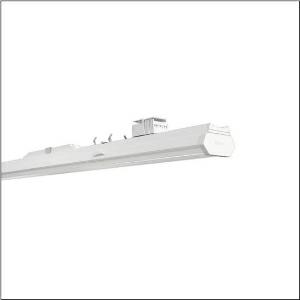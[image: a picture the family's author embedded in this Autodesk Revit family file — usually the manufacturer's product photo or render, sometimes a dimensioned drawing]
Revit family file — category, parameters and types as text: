
# Revit family: licross_r__11_protected_mo_51tp12dn495g3c_6ec9
name_source: partatom
category: Lighting Fixtures
units: mm (PartAtom-declared; Revit-internal decimal feet)

## family parameters
Cut with Voids When Loaded = No
Host = Face
Light Source = No
Part Type = Normal
Room Calculation Point = No
Round Connector Dimension = Use Diameter
Shared = No

## types (1)
- --- (1 x LED, 980 lm, 6.8 W, 4000K)
    Apparent Load = 7 VA
    CIE Flux Codes = 73 92 98 99 100
    Color Rendering = 80
    Color Temperature = 4000K
    Default Elevation = 1800 mm
    Description = Licross® 11 Protected MO, luminaire insert, of sheet steel, galvanised, coil coated, white, length: 1.500mm, width: 90mm, height: 101mm, LED rated luminous flux: 9.980lm, light colour: 840, control gear: DALI 2 (for two DALI lines), with plug, 6-pole, with phase selection, for trunking rail, 14-core, mains connection: 220..240V, AC, 50/60Hz, rated input power: 61W, for trunking rail, 14-core, internal wiring halogen-free, for emergency light function, converter,control gear: single battery element, battery: LiFePO4, 9Ah, primary light control with lens, of plastic, primary optical cover: cover, of PMMA, light emission: direct distribution, primary light characteristic: symmetric, protection rating (complete): IP64, insulation class (complete): insulation class I (protective earthing), certification: CE, UKCA, protection symbol: D if used in an environment with conductive dust loads with corresponding accessories, impact resistance: IK06, permissible ambient temperature for indoor applications: +5..+35°C, standard: EN 60598-2-22, LABS conformity tested according to VDMA 24364:2018-05, reducing of maximum allowable ambient temperature of 5°C with ceiling mounting, corresponds to IFS (International Featured Standards) requirements for safety and quality in the food industry, packaging unit: 1 piece
    Height = 92 mm
    Lamp = 1 x LED
    Lamp Light Flux = 980 lm
    Lamp Power = 6.8 W
    Lamp count = 1
    Length = 1500 mm
    Luminous efficacy = 144 lm/W
    Manufacturer = Siteco
    ModVariant = No
    Model = 51TP12DN495G3C
    Mounting Place = Ceiling
    Mounting Type = Pendant
    Number of Poles = 1
    OnlyDefault = Yes
    Power Factor = 1
    Product Name = Licross® 11 Protected MO
    Product group = luminaire insert | ceiling pendant
    ProductGroupID = 902
    Protection Class = Protection class I
    Protection Degree = IP 64
    RLX_Detail_Level = 1
    RLX_Emergency_Light_Flux = 0 lm
    RLX_Emergency_Type = 0
    RLX_Emergency_Type_DB = No
    RlxData = <blob elided: 24809 chars, md5=9ab4ca81>
    Socket = socket
    Standby Power = 0 W
    System Light Flux = 980 lm
    System Power = 7 W
    Type Comments = : emergency light operation: 3 h
    Type Image = l_1256148.jpg
    URL = http://relux.com
    VarID = @adj_112189
    Voltage = 0 V
    Weight = 0.00 kg
    Width = 88 mm

## geometry (parser evidence)
native form markers: Blend x4, Sweep x10
no freeform markers — native parametric forms only
